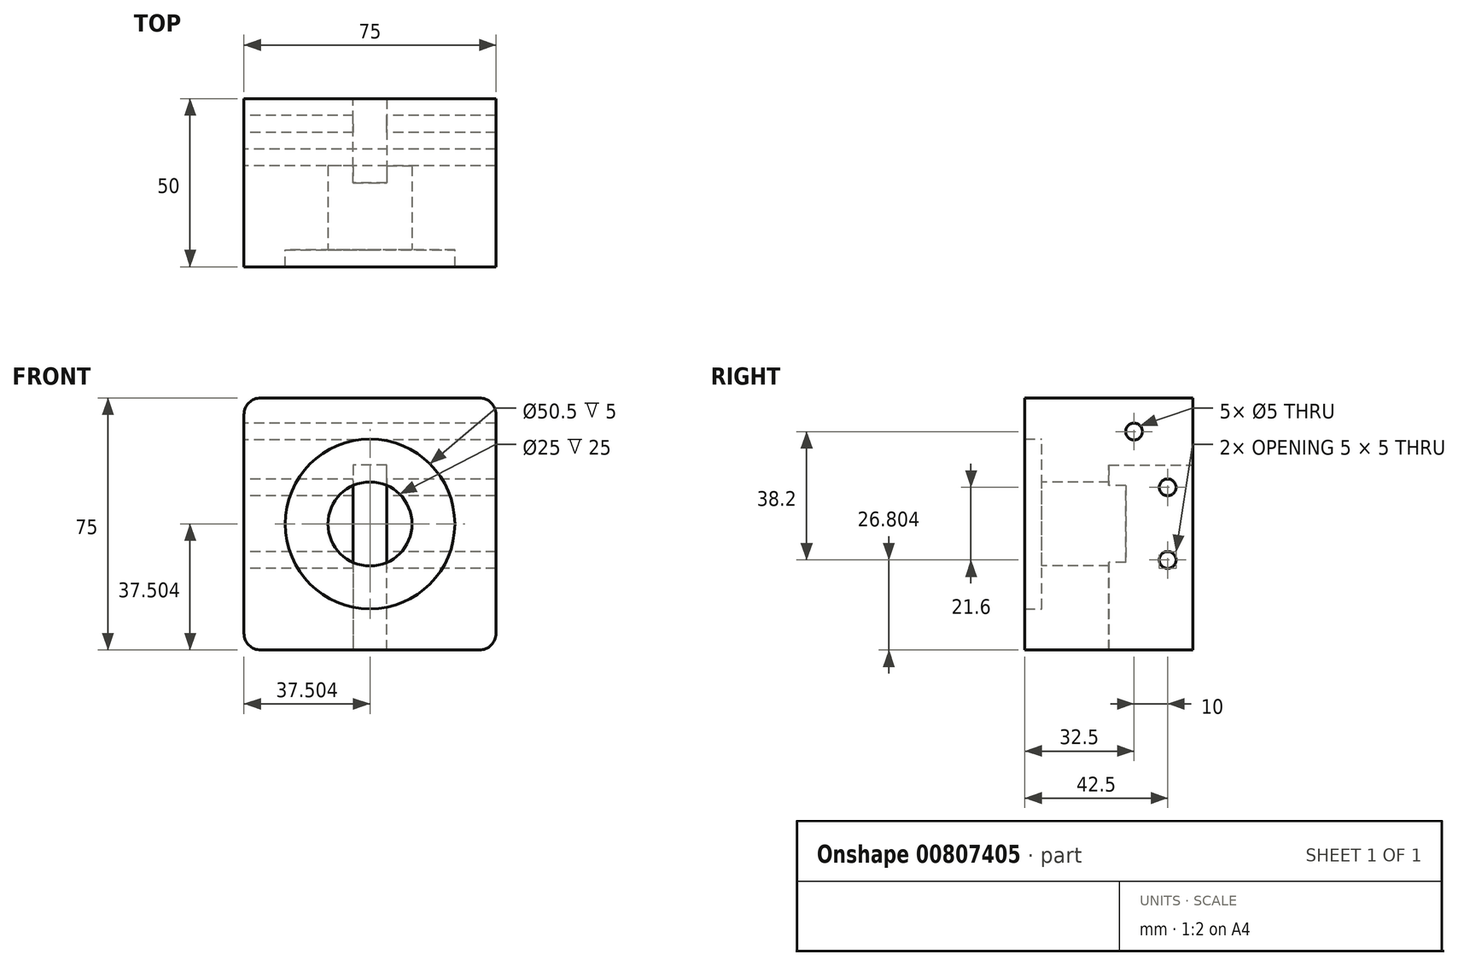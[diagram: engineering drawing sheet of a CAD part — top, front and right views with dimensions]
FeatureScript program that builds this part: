
annotation { "Feature Type Name" : "Feature", "Feature Type Description" : "" }
export const myFeature = defineFeature(function(context is Context, id is Id, definition is map)
    precondition{}
    {
        {
            var Q0;
            Q0=qCreatedBy(makeId("Front.planeOp"),FACE);
            var sketch = newSketch(context, id + "F0", { "sketchPlane" : qUnion([Q0])});
            skLineSegment(sketch, "E0.bottom", {"start": v(-29.62, 20.44) * mm, "end": v(45.38, 20.44) * mm});
            skLineSegment(sketch, "E0.top", {"start": v(-29.62, -54.56) * mm, "end": v(45.38, -54.56) * mm});
            skLineSegment(sketch, "E0.left", {"start": v(-29.62, 20.44) * mm, "end": v(-29.62, -54.56) * mm});
            skLineSegment(sketch, "E0.right", {"start": v(45.38, 20.44) * mm, "end": v(45.38, -54.56) * mm});
            skSolve(sketch);
        }
        {
            var Q0;
            Q0=qSketchRegion(id+"F0",true);
            extrude(context, id + "F1", {"entities" : qUnion([Q0]), "depth" : 45 * mm, "offsetDistance" : 25 * mm});
        }
        {
            var Q0;
            Q0=makeQuery(id+"F1.opExtrude","SWEPT_EDGE",EDGE,{"disambiguationData":[OSD([sQuery(id+"F0.wireOp",EDGE,"E0.bottom"),sQuery(id+"F0.wireOp",EDGE,"E0.left")])]});
            var Q1;
            Q1=makeQuery(id+"F1.opExtrude","SWEPT_EDGE",EDGE,{"disambiguationData":[OSD([sQuery(id+"F0.wireOp",EDGE,"E0.top"),sQuery(id+"F0.wireOp",EDGE,"E0.left")])]});
            var Q2;
            Q2=makeQuery(id+"F1.opExtrude","SWEPT_EDGE",EDGE,{"disambiguationData":[OSD([sQuery(id+"F0.wireOp",EDGE,"E0.top"),sQuery(id+"F0.wireOp",EDGE,"E0.right")])]});
            var Q3;
            Q3=makeQuery(id+"F1.opExtrude","SWEPT_EDGE",EDGE,{"disambiguationData":[OSD([sQuery(id+"F0.wireOp",EDGE,"E0.bottom"),sQuery(id+"F0.wireOp",EDGE,"E0.right")])]});
            fillet(context, id + "F2", {"entities" : qUnion([Q0, Q1, Q2, Q3]), "radius" : 5 * mm, "tangentPropagation" : true, "allowEdgeOverflow" : false});
        }
        {
            var Q0;
            Q0=makeQuery(id+"F1.opExtrude","CAP_FACE",FACE,{"disambiguationData":[OSD([sQuery(id+"F0.wireOp",EDGE,"E0.bottom"),sQuery(id+"F0.wireOp",EDGE,"E0.top"),sQuery(id+"F0.wireOp",EDGE,"E0.left"),sQuery(id+"F0.wireOp",EDGE,"E0.right")])],"isStart":false});
            var sketch = newSketch(context, id + "F3", { "sketchPlane" : qUnion([Q0])});
            skCircle(sketch, "E1", {"center": v(7.88, -17.06) * mm, "radius": 12.5 * mm});
            skPoint(sketch, "E1.centerSnap0", {"position": v(7.88, 20.44) * mm});
            skPoint(sketch, "E1.centerSnap1", {"position": v(-29.62, -17.06) * mm});
            skSolve(sketch);
        }
        {
            var Q0;
            Q0=qSketchRegion(id+"F3",true);
            extrude(context, id + "F4", {"entities" : qUnion([Q0]), "operationType" : NewBodyOperationType.REMOVE, "oppositeDirection" : true, "depth" : 25 * mm, "offsetDistance" : 25 * mm});
        }
        {
            var Q0;
            Q0=makeQuery(id+"F1.opExtrude","CAP_FACE",FACE,{"disambiguationData":[OSD([sQuery(id+"F0.wireOp",EDGE,"E0.bottom"),sQuery(id+"F0.wireOp",EDGE,"E0.top"),sQuery(id+"F0.wireOp",EDGE,"E0.left"),sQuery(id+"F0.wireOp",EDGE,"E0.right")])],"isStart":false});
            var sketch = newSketch(context, id + "F5", { "sketchPlane" : qUnion([Q0])});
            skLineSegment(sketch, "E2", {"start": v(7.88, 20.44) * mm, "end": v(7.88, -4.56) * mm});
            skLineSegment(sketch, "E3", {"start": v(7.88, 20.44) * mm, "end": v(2.88, 20.44) * mm});
            skLineSegment(sketch, "E4", {"start": v(2.88, 20.44) * mm, "end": v(2.88, 20.44) * mm});
            skLineSegment(sketch, "E5", {"start": v(2.88, 20.44) * mm, "end": v(12.88, 20.44) * mm});
            skLineSegment(sketch, "E6", {"start": v(12.88, 20.44) * mm, "end": v(12.88, 20.44) * mm});
            skLineSegment(sketch, "E7", {"start": v(7.88, 20.44) * mm, "end": v(12.88, 20.44) * mm});
            skCircle(sketch, "E8", {"center": v(7.88, -17.06) * mm, "radius": 25.25 * mm});
            skSolve(sketch);
        }
        {
            var Q0;
            Q0=makeQuery(id+"F0.imprint","IMPRINT",FACE,{"disambiguationData":[TD([[makeQuery(id+"F0.imprint","IMPRINT",EDGE,{"derivedFrom":sQuery(id+"F0.wireOp",EDGE,"E0.bottom")}),-1.0]])]});
            var sketch = newSketch(context, id + "F6", { "sketchPlane" : qUnion([Q0])});
            skLineSegment(sketch, "E9", {"start": v(2.87, 0.44) * mm, "end": v(2.87, -54.64) * mm});
            skLineSegment(sketch, "E10", {"start": v(2.87, -54.64) * mm, "end": v(12.87, -54.64) * mm});
            skLineSegment(sketch, "E11", {"start": v(12.87, -54.64) * mm, "end": v(12.87, 0.5) * mm});
            skLineSegment(sketch, "E12", {"start": v(12.87, 0.5) * mm, "end": v(2.87, 0.44) * mm});
            skSolve(sketch);
        }
        {
            var Q0;
            Q0=qSketchRegion(id+"F6",true);
            extrude(context, id + "F7", {"entities" : qUnion([Q0]), "operationType" : NewBodyOperationType.REMOVE, "depth" : 25 * mm, "offsetDistance" : 25 * mm});
        }
        {
            var Q0;
            Q0=makeQuery(id+"F1.opExtrude","SWEPT_FACE",FACE,{"disambiguationData":[OSD([sQuery(id+"F0.wireOp",EDGE,"E0.left")])]});
            var sketch = newSketch(context, id + "F8", { "sketchPlane" : qUnion([Q0])});
            skLineSegment(sketch, "E13", {"start": v(0, 15.44) * mm, "end": v(0, -6.16) * mm});
            skLineSegment(sketch, "E14", {"start": v(0, -6.16) * mm, "end": v(0, -27.76) * mm});
            skLineSegment(sketch, "E15", {"start": v(0, -27.76) * mm, "end": v(7.5, -27.76) * mm});
            skLineSegment(sketch, "E16", {"start": v(0, -6.16) * mm, "end": v(7.5, -6.16) * mm});
            skCircle(sketch, "E17", {"center": v(7.5, -6.16) * mm, "radius": 2.5 * mm});
            skCircle(sketch, "E18", {"center": v(7.5, -27.76) * mm, "radius": 2.5 * mm});
            skSolve(sketch);
        }
        {
            var Q0;
            Q0=qSketchRegion(id+"F8",true);
            extrude(context, id + "F9", {"entities" : qUnion([Q0]), "operationType" : NewBodyOperationType.REMOVE, "endBound" : BoundingType.THROUGH_ALL, "oppositeDirection" : true, "depth" : 25 * mm, "offsetDistance" : 25 * mm});
        }
        {
            var Q0;
            Q0=makeQuery(id+"F1.opExtrude","CAP_FACE",FACE,{"disambiguationData":[OSD([sQuery(id+"F0.wireOp",EDGE,"E0.bottom"),sQuery(id+"F0.wireOp",EDGE,"E0.top"),sQuery(id+"F0.wireOp",EDGE,"E0.left"),sQuery(id+"F0.wireOp",EDGE,"E0.right")])],"isStart":false});
            extrude(context, id + "F10", {"entities" : qUnion([Q0]), "operationType" : NewBodyOperationType.ADD, "depth" : 25 * mm, "offsetDistance" : 25 * mm});
        }
        {
            var Q0;
            {var subQ0=sQuery(id+"F0.wireOp",EDGE,"E0.left");Q0=makeQuery(id+"F10.boolean.opBoolean","MERGE",FACE,{"derivedFrom":[makeQuery(id+"F1.opExtrude","SWEPT_FACE",FACE,{"disambiguationData":[OSD([subQ0])]}),makeQuery(id+"F10.opExtrude","SWEPT_FACE",FACE,{"disambiguationData":[OSD([subQ0])]})]});}
            var sketch = newSketch(context, id + "F11", { "sketchPlane" : qUnion([Q0])});
            skLineSegment(sketch, "E19", {"start": v(0, 15.44) * mm, "end": v(35, 15.44) * mm});
            skLineSegment(sketch, "E20", {"start": v(35, 15.44) * mm, "end": v(17.5, 15.44) * mm});
            skLineSegment(sketch, "E21", {"start": v(17.5, 15.44) * mm, "end": v(52.5, 15.44) * mm});
            skLineSegment(sketch, "E22", {"start": v(52.5, 15.44) * mm, "end": v(52.5, 10.44) * mm});
            skLineSegment(sketch, "E23", {"start": v(52.5, 10.44) * mm, "end": v(17.5, 10.44) * mm});
            skCircle(sketch, "E24", {"center": v(17.5, 10.44) * mm, "radius": 2.5 * mm});
            skCircle(sketch, "E25", {"center": v(52.5, 10.44) * mm, "radius": 2.5 * mm});
            skSolve(sketch);
        }
        {
            var Q0;
            Q0=qSketchRegion(id+"F11",true);
            extrude(context, id + "F12", {"entities" : qUnion([Q0]), "operationType" : NewBodyOperationType.REMOVE, "endBound" : BoundingType.THROUGH_ALL, "oppositeDirection" : true, "depth" : 25 * mm, "offsetDistance" : 25 * mm});
        }
        {
            var Q0;
            Q0 = qSketchRegion(id + "F5", true);
            extrude(context, id + "F13", {"entities" : qUnion([Q0]), "operationType" : NewBodyOperationType.REMOVE, "depth" : 25 * mm, "offsetDistance" : 25 * mm});
        }
        {
            var Q0;
            Q0=makeQuery(id+"F10.opExtrude","CAP_FACE",FACE,{"disambiguationData":[OSD([sQuery(id+"F0.wireOp",EDGE,"E0.bottom"),sQuery(id+"F0.wireOp",EDGE,"E0.top"),sQuery(id+"F0.wireOp",EDGE,"E0.left"),sQuery(id+"F0.wireOp",EDGE,"E0.right")])],"isStart":false});
            extrude(context, id + "F14", {"entities" : qUnion([Q0]), "operationType" : NewBodyOperationType.REMOVE, "oppositeDirection" : true, "depth" : 20 * mm, "offsetDistance" : 25 * mm});
        }
    });
